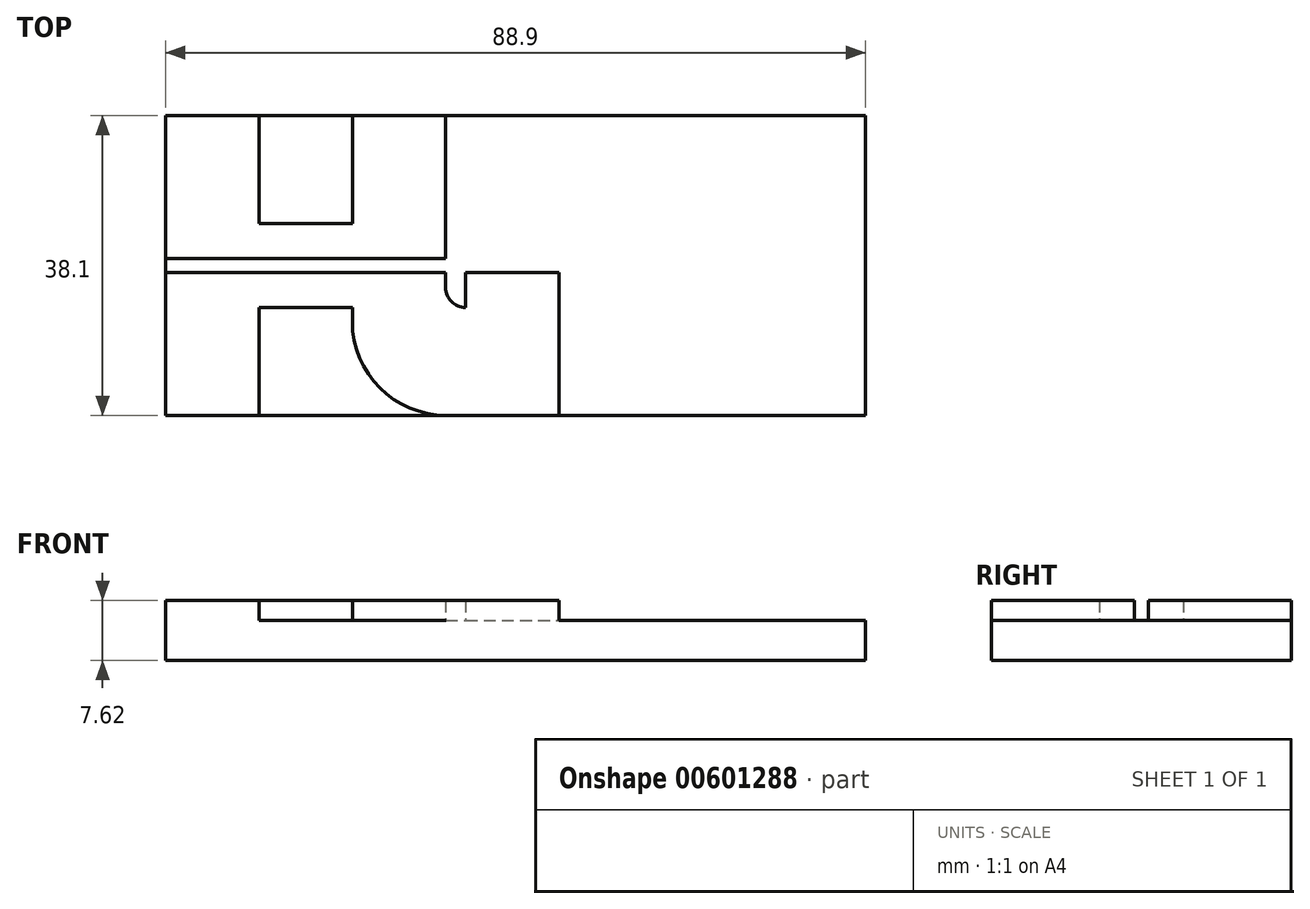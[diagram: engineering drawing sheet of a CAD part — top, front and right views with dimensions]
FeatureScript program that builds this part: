
annotation { "Feature Type Name" : "Feature", "Feature Type Description" : "" }
export const myFeature = defineFeature(function(context is Context, id is Id, definition is map)
    precondition{}
    {
        {
            var Q0;
            Q0=qCreatedBy(makeId("Top.planeOp"),FACE);
            var sketch = newSketch(context, id + "F0", { "sketchPlane" : qUnion([Q0])});
            skLineSegment(sketch, "E0.bottom", {"start": v(44.45, -19.05) * mm, "end": v(-44.45, -19.05) * mm});
            skLineSegment(sketch, "E0.top", {"start": v(44.45, 19.05) * mm, "end": v(-44.45, 19.05) * mm});
            skLineSegment(sketch, "E0.left", {"start": v(44.45, -19.05) * mm, "end": v(44.45, 19.05) * mm});
            skLineSegment(sketch, "E0.right", {"start": v(-44.45, -19.05) * mm, "end": v(-44.45, 19.05) * mm});
            skPoint(sketch, "E0.middle", {"position": v(0, 0) * mm});
            skSolve(sketch);
        }
        {
            var Q0;
            Q0=makeQuery(id+"F0.imprint","IMPRINT",FACE,{"disambiguationData":[TD([[makeQuery(id+"F0.imprint","IMPRINT",EDGE,{"derivedFrom":sQuery(id+"F0.wireOp",EDGE,"E0.bottom")}),-1.0]])]});
            extrude(context, id + "F1", {"entities" : qUnion([Q0]), "depth" : 5.08 * mm, "offsetDistance" : 25.4 * mm});
        }
        {
            var Q0;
            Q0=makeQuery(id+"F1.opExtrude","CAP_FACE",FACE,{"disambiguationData":[OSD([sQuery(id+"F0.wireOp",EDGE,"E0.bottom"),sQuery(id+"F0.wireOp",EDGE,"E0.top"),sQuery(id+"F0.wireOp",EDGE,"E0.left"),sQuery(id+"F0.wireOp",EDGE,"E0.right")])],"isStart":false});
            var sketch = newSketch(context, id + "F2", { "sketchPlane" : qUnion([Q0])});
            skLineSegment(sketch, "E1", {"start": v(-44.45, 16.5) * mm, "end": v(-44.45, 0.89) * mm});
            skLineSegment(sketch, "E2", {"start": v(-44.45, 0.89) * mm, "end": v(-36.17, 0.89) * mm});
            skLineSegment(sketch, "E3", {"start": v(-36.17, 0.89) * mm, "end": v(-8.87, 0.89) * mm});
            skLineSegment(sketch, "E4", {"start": v(-8.87, 0.89) * mm, "end": v(-8.87, 16.51) * mm});
            skLineSegment(sketch, "E5", {"start": v(-11.41, 19.05) * mm, "end": v(-20.73, 19.05) * mm});
            skLineSegment(sketch, "E6", {"start": v(-20.73, 19.05) * mm, "end": v(-20.73, 5.33) * mm});
            skLineSegment(sketch, "E7", {"start": v(-20.73, 5.33) * mm, "end": v(-32.59, 5.33) * mm});
            skLineSegment(sketch, "E8", {"start": v(-32.59, 5.33) * mm, "end": v(-32.59, 19.05) * mm});
            skLineSegment(sketch, "E9", {"start": v(-32.59, 19.05) * mm, "end": v(-41.91, 19.05) * mm});
            skLineSegment(sketch, "E10", {"start": v(-44.45, -0.89) * mm, "end": v(-44.45, -19.05) * mm});
            skLineSegment(sketch, "E11", {"start": v(-44.45, -19.05) * mm, "end": v(-32.59, -19.05) * mm});
            skLineSegment(sketch, "E12", {"start": v(-32.59, -19.05) * mm, "end": v(-32.59, -5.33) * mm});
            skLineSegment(sketch, "E13", {"start": v(-32.59, -5.33) * mm, "end": v(-20.73, -5.33) * mm});
            skLineSegment(sketch, "E14", {"start": v(-20.73, -5.33) * mm, "end": v(-20.73, -7.11) * mm});
            skLineSegment(sketch, "E15", {"start": v(-8.8, -19.05) * mm, "end": v(5.53, -19.05) * mm});
            skLineSegment(sketch, "E16", {"start": v(-44.45, -0.89) * mm, "end": v(-8.87, -0.89) * mm});
            skLineSegment(sketch, "E17", {"start": v(-6.33, -5.33) * mm, "end": v(-6.33, -0.89) * mm});
            skLineSegment(sketch, "E18", {"start": v(-6.33, -0.89) * mm, "end": v(5.53, -0.89) * mm});
            skLineSegment(sketch, "E19", {"start": v(5.53, -0.89) * mm, "end": v(5.53, -19.05) * mm});
            skPoint(sketch, "E20.visualSharp", {"position": v(-44.45, 19.05) * mm});
            skPoint(sketch, "E21.visualSharp", {"position": v(-8.87, -5.33) * mm});
            skLineSegment(sketch, "E22", {"start": v(-44.45, 16.5) * mm, "end": v(-44.45, 19.05) * mm});
            skLineSegment(sketch, "E23", {"start": v(-41.91, 19.05) * mm, "end": v(-44.45, 19.05) * mm});
            skPoint(sketch, "E24.visualSharp", {"position": v(-20.73, -19.05) * mm});
            skArc(sketch, "E24.filletArc", {"start": v(-20.73, -7.11) * mm, "mid": v(-17.24, -15.55) * mm, "end": v(-8.8, -19.05) * mm});
            skLineSegment(sketch, "E25", {"start": v(-8.87, -0.89) * mm, "end": v(-8.87, -2.8) * mm});
            skLineSegment(sketch, "E26", {"start": v(-6.33, -5.33) * mm, "end": v(-6.33, -5.33) * mm});
            skPoint(sketch, "E27.visualSharp", {"position": v(-8.87, 19.05) * mm});
            skLineSegment(sketch, "E28", {"start": v(-11.41, 19.05) * mm, "end": v(-8.87, 19.05) * mm});
            skLineSegment(sketch, "E29", {"start": v(-8.87, 16.51) * mm, "end": v(-8.87, 19.05) * mm});
            skArc(sketch, "E30.filletArc", {"start": v(-8.87, -2.8) * mm, "mid": v(-8.13, -4.6) * mm, "end": v(-6.33, -5.33) * mm});
            skLineSegment(sketch, "E31.bottom", {"start": v(-6.33, 0.89) * mm, "end": v(5.53, 0.89) * mm});
            skLineSegment(sketch, "E31.top", {"start": v(-6.33, 19.05) * mm, "end": v(5.53, 19.05) * mm});
            skLineSegment(sketch, "E31.left", {"start": v(-6.33, 0.89) * mm, "end": v(-6.33, 19.05) * mm});
            skPoint(sketch, "E32", {"position": v(5.53, 9.97) * mm});
            skLineSegment(sketch, "E33", {"start": v(5.53, 0.89) * mm, "end": v(5.53, 9.97) * mm});
            skLineSegment(sketch, "E34", {"start": v(5.53, 9.97) * mm, "end": v(17.4, 9.97) * mm});
            skSolve(sketch);
        }
        {
            var Q0;
            Q0=makeQuery(id+"F2.imprint","IMPRINT",FACE,{"disambiguationData":[TD([[makeQuery(id+"F2.imprint","IMPRINT",EDGE,{"derivedFrom":sQuery(id+"F2.wireOp",EDGE,"E1")}),-1.0]])]});
            var Q1;
            Q1=makeQuery(id+"F2.imprint","IMPRINT",FACE,{"disambiguationData":[TD([[makeQuery(id+"F2.imprint","IMPRINT",EDGE,{"derivedFrom":sQuery(id+"F2.wireOp",EDGE,"E10")}),-1.0]])]});
            extrude(context, id + "F3", {"entities" : qUnion([Q0, Q1]), "operationType" : NewBodyOperationType.ADD, "depth" : 2.54 * mm, "offsetDistance" : 25.4 * mm});
        }
    });
